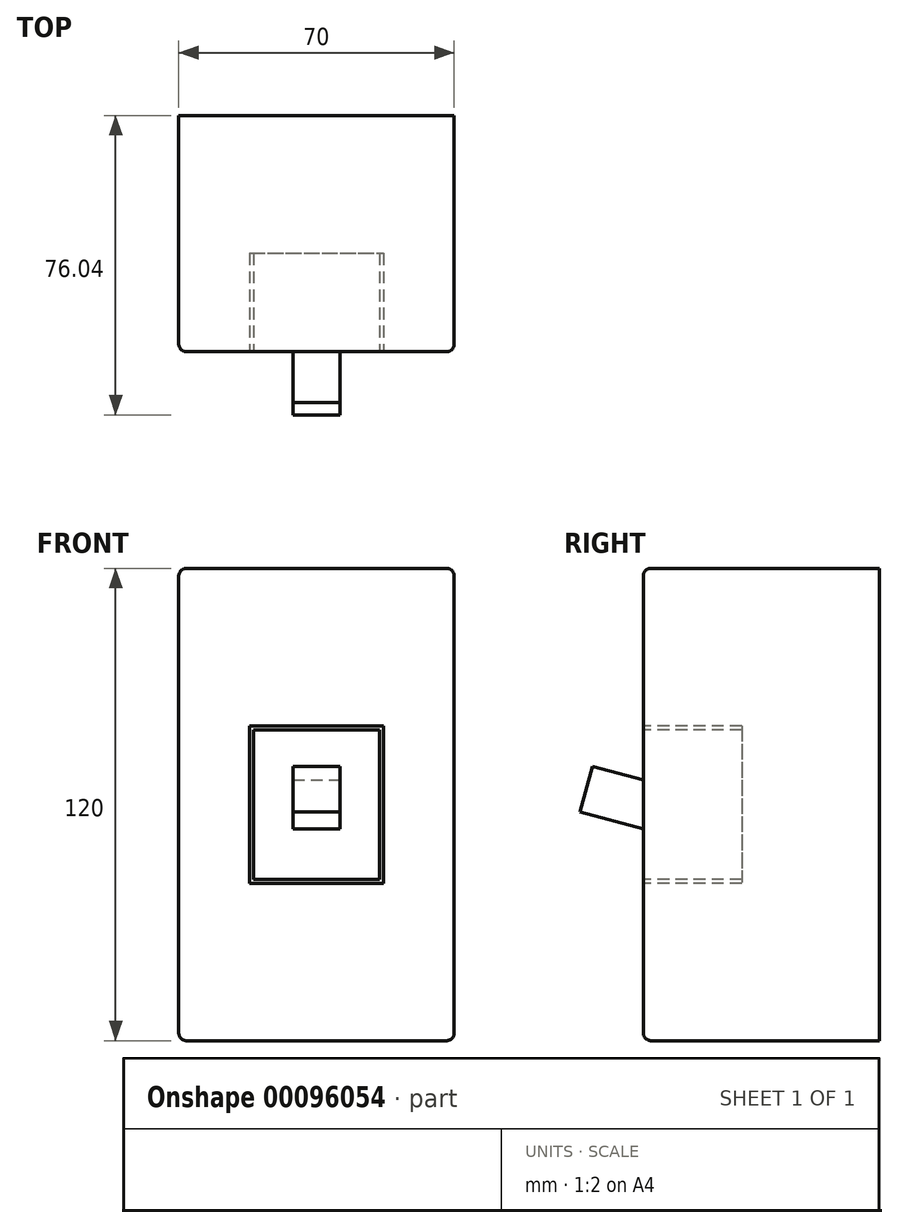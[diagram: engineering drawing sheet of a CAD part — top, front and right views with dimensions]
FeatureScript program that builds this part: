
annotation { "Feature Type Name" : "Feature", "Feature Type Description" : "" }
export const myFeature = defineFeature(function(context is Context, id is Id, definition is map)
    precondition{}
    {
        {
            var Q0;
            Q0=qCreatedBy(makeId("Front.planeOp"),FACE);
            var sketch = newSketch(context, id + "F0", { "sketchPlane" : qUnion([Q0])});
            skLineSegment(sketch, "E0.bottom", {"start": v(35, -60) * mm, "end": v(-35, -60) * mm});
            skLineSegment(sketch, "E0.top", {"start": v(35, 60) * mm, "end": v(-35, 60) * mm});
            skLineSegment(sketch, "E0.left", {"start": v(35, -60) * mm, "end": v(35, 60) * mm});
            skLineSegment(sketch, "E0.right", {"start": v(-35, -60) * mm, "end": v(-35, 60) * mm});
            skPoint(sketch, "E0.middle", {"position": v(0, 0) * mm});
            skSolve(sketch);
        }
        {
            var Q0;
            Q0=qSketchRegion(id+"F0",true);
            extrude(context, id + "F1", {"entities" : qUnion([Q0]), "depth" : 60 * mm});
        }
        {
            var Q0;
            Q0=makeQuery(id+"F1.opExtrude","SWEPT_EDGE",EDGE,{"disambiguationData":[OSD([sQuery(id+"F0.wireOp",EDGE,"E0.top"),sQuery(id+"F0.wireOp",EDGE,"E0.left")])]});
            var Q1;
            Q1=makeQuery(id+"F1.opExtrude","SWEPT_EDGE",EDGE,{"disambiguationData":[OSD([sQuery(id+"F0.wireOp",EDGE,"E0.bottom"),sQuery(id+"F0.wireOp",EDGE,"E0.left")])]});
            var Q2;
            Q2=makeQuery(id+"F1.opExtrude","SWEPT_EDGE",EDGE,{"disambiguationData":[OSD([sQuery(id+"F0.wireOp",EDGE,"E0.top"),sQuery(id+"F0.wireOp",EDGE,"E0.right")])]});
            var Q3;
            Q3=makeQuery(id+"F1.opExtrude","SWEPT_EDGE",EDGE,{"disambiguationData":[OSD([sQuery(id+"F0.wireOp",EDGE,"E0.bottom"),sQuery(id+"F0.wireOp",EDGE,"E0.right")])]});
            var Q4;
            Q4=makeQuery(id+"F1.opExtrude","CAP_FACE",FACE,{"disambiguationData":[OSD([sQuery(id+"F0.wireOp",EDGE,"E0.bottom"),sQuery(id+"F0.wireOp",EDGE,"E0.top"),sQuery(id+"F0.wireOp",EDGE,"E0.left"),sQuery(id+"F0.wireOp",EDGE,"E0.right")])],"isStart":false});
            fillet(context, id + "F2", {"entities" : qUnion([Q0, Q1, Q2, Q3, Q4]), "radius" : 2 * mm, "tangentPropagation" : true, "allowEdgeOverflow" : false});
        }
        {
            var Q0;
            Q0=makeQuery(id+"F1.opExtrude","CAP_FACE",FACE,{"disambiguationData":[OSD([sQuery(id+"F0.wireOp",EDGE,"E0.bottom"),sQuery(id+"F0.wireOp",EDGE,"E0.top"),sQuery(id+"F0.wireOp",EDGE,"E0.left"),sQuery(id+"F0.wireOp",EDGE,"E0.right")])],"isStart":false});
            var sketch = newSketch(context, id + "F3", { "sketchPlane" : qUnion([Q0])});
            skLineSegment(sketch, "E1.bottom", {"start": v(-17, 20) * mm, "end": v(17, 20) * mm});
            skLineSegment(sketch, "E1.top", {"start": v(-17, -20) * mm, "end": v(17, -20) * mm});
            skLineSegment(sketch, "E1.left", {"start": v(-17, 20) * mm, "end": v(-17, -20) * mm});
            skLineSegment(sketch, "E1.right", {"start": v(17, 20) * mm, "end": v(17, -20) * mm});
            skLineSegment(sketch, "E2.0", {"start": v(-16, 19) * mm, "end": v(16, 19) * mm});
            skLineSegment(sketch, "E2.1", {"start": v(-16, 19) * mm, "end": v(-16, -19) * mm});
            skLineSegment(sketch, "E2.2", {"start": v(-16, -19) * mm, "end": v(16, -19) * mm});
            skLineSegment(sketch, "E2.3", {"start": v(16, 19) * mm, "end": v(16, -19) * mm});
            skSolve(sketch);
        }
        {
            var Q0;
            Q0=qSketchRegion(id+"F3",true);
            extrude(context, id + "F4", {"entities" : qUnion([Q0]), "operationType" : NewBodyOperationType.REMOVE, "oppositeDirection" : true, "depth" : 25 * mm});
        }
        {
            var Q0;
            Q0=makeQuery(id+"F4.boolean.opBoolean","SPLIT",FACE,{"disambiguationData":[TD([makeQuery(id+"F4.opExtrude","SWEPT_FACE",FACE,{"disambiguationData":[OSD([sQuery(id+"F3.wireOp",EDGE,"E2.0")])]})])],"derivedFrom":makeQuery(id+"F1.opExtrude","CAP_FACE",FACE,{"disambiguationData":[OSD([sQuery(id+"F0.wireOp",EDGE,"E0.bottom"),sQuery(id+"F0.wireOp",EDGE,"E0.top"),sQuery(id+"F0.wireOp",EDGE,"E0.left"),sQuery(id+"F0.wireOp",EDGE,"E0.right")])],"isStart":false})});
            var sketch = newSketch(context, id + "F5", { "sketchPlane" : qUnion([Q0])});
            skLineSegment(sketch, "E3", {"start": v(22.74, 0) * mm, "end": v(-26.04, 0) * mm});
            skPoint(sketch, "E3.startSnap0", {"position": v(16, 0) * mm});
            skPoint(sketch, "E3.endSnap0", {"position": v(16, 0) * mm});
            skSolve(sketch);
        }
        {
            var Q0;
            Q0=sQuery(id+"F5.wireOp",EDGE,"E3");
            var Q1;
            {var subQ5=makeQuery(id+"F4.boolean.opBoolean","COPY",EDGE,{"derivedFrom":makeQuery(id+"F4.opExtrude","CAP_EDGE",EDGE,{"disambiguationData":[OSD([sQuery(id+"F3.wireOp",EDGE,"E2.2")])],"isStart":true})});Q1=makeQuery(id+"F5.imprint","IMPRINT",FACE,{"disambiguationData":[TD([[makeQuery(id+"F5.imprint","IMPRINT",EDGE,{"derivedFrom":subQ5}),1.0]])]});}
            cPlane(context, id + "F6", {"entities" : qUnion([Q0, Q1]), "cplaneType" : CPlaneType.LINE_ANGLE, "offset" : 150 * mm, "angle" : 15 * degree, "width" : 150 * mm, "height" : 150 * mm});
        }
        {
            var Q0;
            Q0=qCreatedBy(id+"F6.planeOp",FACE);
            var sketch = newSketch(context, id + "F7", { "sketchPlane" : qUnion([Q0])});
            skLineSegment(sketch, "E4.bottom", {"start": v(6, -9.53) * mm, "end": v(-6, -9.53) * mm});
            skLineSegment(sketch, "E4.top", {"start": v(6, -21.53) * mm, "end": v(-6, -21.53) * mm});
            skLineSegment(sketch, "E4.left", {"start": v(6, -9.53) * mm, "end": v(6, -21.53) * mm});
            skLineSegment(sketch, "E4.right", {"start": v(-6, -9.53) * mm, "end": v(-6, -21.53) * mm});
            skSolve(sketch);
        }
        {
            var Q0;
            Q0 = qSketchRegion(id + "F7", true);
            extrude(context, id + "F8", {"entities" : qUnion([Q0]), "operationType" : NewBodyOperationType.ADD, "endBound" : BoundingType.SYMMETRIC, "depth" : 30 * mm});
        }
    });
